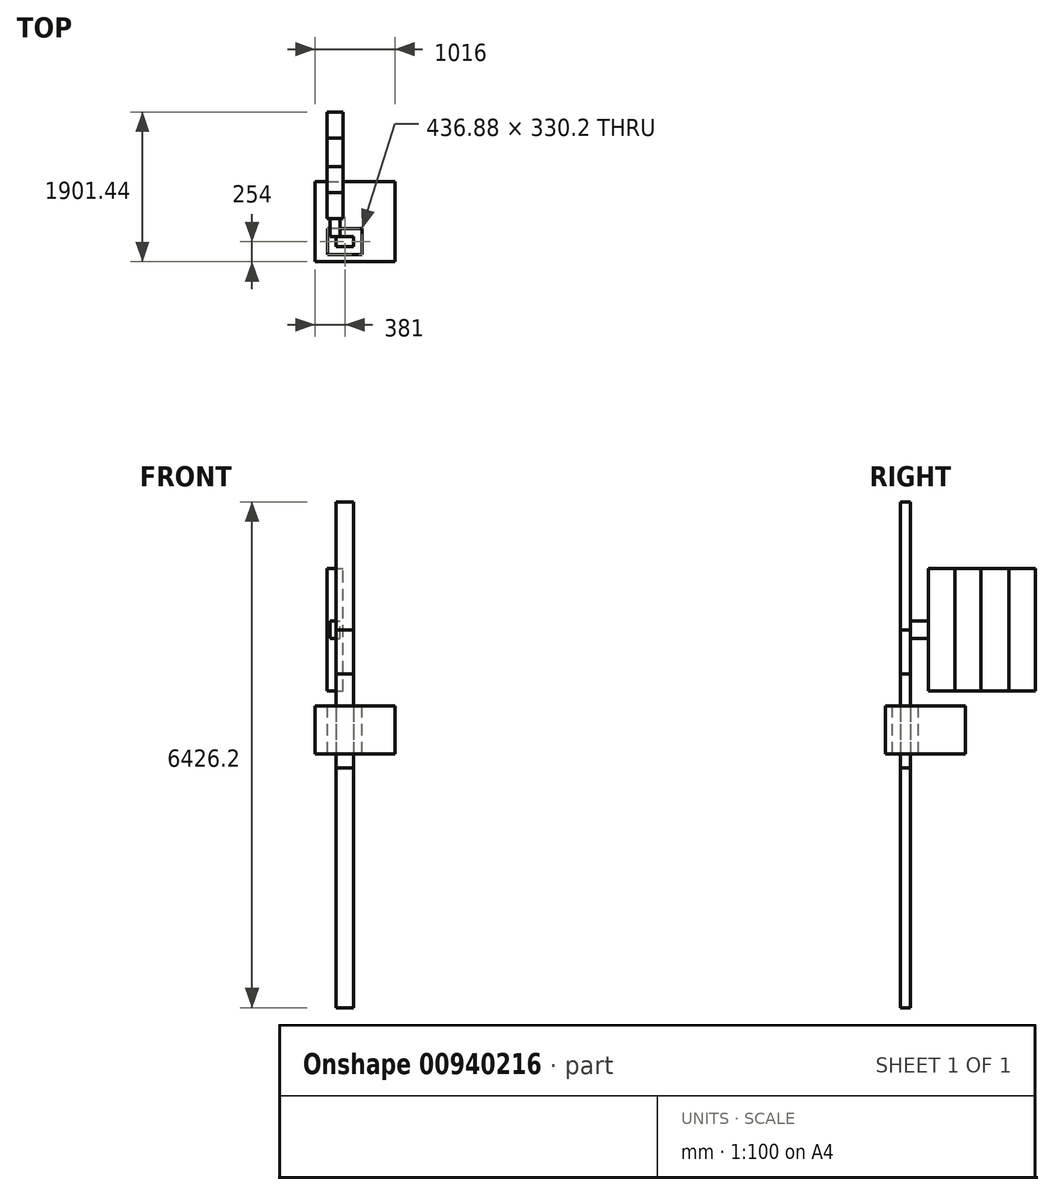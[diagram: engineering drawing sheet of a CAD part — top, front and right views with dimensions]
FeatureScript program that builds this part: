
annotation { "Feature Type Name" : "Feature", "Feature Type Description" : "" }
export const myFeature = defineFeature(function(context is Context, id is Id, definition is map)
    precondition{}
    {
        {
            var Q0;
            Q0=qCreatedBy(makeId("Top.planeOp"),FACE);
            var sketch = newSketch(context, id + "F0", { "sketchPlane" : qUnion([Q0])});
            skLineSegment(sketch, "E0.bottom", {"start": v(0, 0) * mm, "end": v(1016, 0) * mm});
            skLineSegment(sketch, "E0.top", {"start": v(0, 1016) * mm, "end": v(1016, 1016) * mm});
            skLineSegment(sketch, "E0.left", {"start": v(0, 0) * mm, "end": v(0, 1016) * mm});
            skLineSegment(sketch, "E0.right", {"start": v(1016, 0) * mm, "end": v(1016, 1016) * mm});
            skSolve(sketch);
        }
        {
            var Q0;
            Q0=makeQuery(id+"F0.imprint","IMPRINT",FACE,{"disambiguationData":[TD([[makeQuery(id+"F0.imprint","IMPRINT",EDGE,{"derivedFrom":sQuery(id+"F0.wireOp",EDGE,"E0.bottom")}),1.0]])]});
            extrude(context, id + "F1", {"entities" : qUnion([Q0]), "depth" : 609.6 * mm, "offsetDistance" : 25.4 * mm});
        }
        {
            var Q0;
            Q0=makeQuery(id+"F1.opExtrude","CAP_FACE",FACE,{"disambiguationData":[OSD([sQuery(id+"F0.wireOp",EDGE,"E0.bottom"),sQuery(id+"F0.wireOp",EDGE,"E0.top"),sQuery(id+"F0.wireOp",EDGE,"E0.left"),sQuery(id+"F0.wireOp",EDGE,"E0.right")])],"isStart":false});
            var sketch = newSketch(context, id + "F2", { "sketchPlane" : qUnion([Q0])});
            skLineSegment(sketch, "E1.bottom", {"start": v(0, 0) * mm, "end": v(381, 0) * mm, "construction": true});
            skLineSegment(sketch, "E1.top", {"start": v(0, 254) * mm, "end": v(381, 254) * mm, "construction": true});
            skLineSegment(sketch, "E1.left", {"start": v(0, 0) * mm, "end": v(0, 254) * mm, "construction": true});
            skLineSegment(sketch, "E1.right", {"start": v(381, 0) * mm, "end": v(381, 254) * mm, "construction": true});
            skLineSegment(sketch, "E2.bottom", {"start": v(491.5, 317.5) * mm, "end": v(270.51, 317.5) * mm});
            skLineSegment(sketch, "E2.top", {"start": v(491.5, 190.5) * mm, "end": v(270.51, 190.5) * mm});
            skLineSegment(sketch, "E2.left", {"start": v(491.5, 317.5) * mm, "end": v(491.5, 190.5) * mm});
            skLineSegment(sketch, "E2.right", {"start": v(270.51, 317.5) * mm, "end": v(270.51, 190.5) * mm});
            skPoint(sketch, "E2.middle", {"position": v(381, 254) * mm});
            skLineSegment(sketch, "E3.bottom", {"start": v(599.44, 419.1) * mm, "end": v(162.56, 419.1) * mm});
            skLineSegment(sketch, "E3.top", {"start": v(599.44, 88.9) * mm, "end": v(162.56, 88.9) * mm});
            skLineSegment(sketch, "E3.left", {"start": v(599.44, 419.1) * mm, "end": v(599.44, 88.9) * mm});
            skLineSegment(sketch, "E3.right", {"start": v(162.56, 419.1) * mm, "end": v(162.56, 88.9) * mm});
            skSolve(sketch);
        }
        {
            var Q0;
            Q0=makeQuery(id+"F2.imprint","IMPRINT",FACE,{"disambiguationData":[TD([[makeQuery(id+"F2.imprint","IMPRINT",EDGE,{"derivedFrom":sQuery(id+"F2.wireOp",EDGE,"E2.bottom")}),-1.0]])]});
            var Q1;
            Q1=makeQuery(id+"F2.imprint","IMPRINT",FACE,{"disambiguationData":[TD([[makeQuery(id+"F2.imprint","IMPRINT",EDGE,{"derivedFrom":sQuery(id+"F2.wireOp",EDGE,"E2.bottom")}),1.0]])]});
            extrude(context, id + "F3", {"entities" : qUnion([Q0, Q1]), "operationType" : NewBodyOperationType.REMOVE, "endBound" : BoundingType.THROUGH_ALL, "oppositeDirection" : true, "depth" : 25.4 * mm, "offsetDistance" : 25.4 * mm});
        }
        {
            var Q0;
            Q0=makeQuery(id+"F2.imprint","IMPRINT",FACE,{"disambiguationData":[TD([[makeQuery(id+"F2.imprint","IMPRINT",EDGE,{"derivedFrom":sQuery(id+"F2.wireOp",EDGE,"E2.bottom")}),1.0]])]});
            extrude(context, id + "F4", {"entities" : qUnion([Q0]), "depth" : 1524 * mm, "offsetDistance" : 25.4 * mm, "symmetric" : true});
        }
        {
            var Q0;
            Q0=makeQuery(id+"F4.opExtrude","CAP_FACE",FACE,{"disambiguationData":[OSD([sQuery(id+"F2.wireOp",EDGE,"E2.bottom"),sQuery(id+"F2.wireOp",EDGE,"E2.top"),sQuery(id+"F2.wireOp",EDGE,"E2.left"),sQuery(id+"F2.wireOp",EDGE,"E2.right")])],"isStart":true});
            extrude(context, id + "F5", {"entities" : qUnion([Q0]), "operationType" : NewBodyOperationType.ADD, "depth" : 1168.4 * mm, "offsetDistance" : 25.4 * mm});
        }
        {
            var Q0;
            Q0=makeQuery(id+"F4.opExtrude","CAP_FACE",FACE,{"disambiguationData":[OSD([sQuery(id+"F2.wireOp",EDGE,"E2.bottom"),sQuery(id+"F2.wireOp",EDGE,"E2.top"),sQuery(id+"F2.wireOp",EDGE,"E2.left"),sQuery(id+"F2.wireOp",EDGE,"E2.right")])],"isStart":false});
            extrude(context, id + "F6", {"entities" : qUnion([Q0]), "operationType" : NewBodyOperationType.ADD, "depth" : 431.8 * mm, "offsetDistance" : 25.4 * mm});
        }
        {
            var Q0;
            Q0=makeQuery(id+"F6.opExtrude","CAP_FACE",FACE,{"disambiguationData":[OSD([sQuery(id+"F2.wireOp",EDGE,"E2.bottom"),sQuery(id+"F2.wireOp",EDGE,"E2.top"),sQuery(id+"F2.wireOp",EDGE,"E2.left"),sQuery(id+"F2.wireOp",EDGE,"E2.right")])],"isStart":false});
            var Q1;
            Q1=makeQuery(id+"F1.opExtrude","CAP_FACE",FACE,{"disambiguationData":[OSD([sQuery(id+"F0.wireOp",EDGE,"E0.bottom"),sQuery(id+"F0.wireOp",EDGE,"E0.top"),sQuery(id+"F0.wireOp",EDGE,"E0.left"),sQuery(id+"F0.wireOp",EDGE,"E0.right")])],"isStart":false});
            extrude(context, id + "F7", {"entities" : qUnion([Q0]), "operationType" : NewBodyOperationType.REMOVE, "endBound" : BoundingType.UP_TO_SURFACE, "oppositeDirection" : true, "depth" : 25.4 * mm, "endBoundEntityFace" : qUnion([Q1]), "offsetDistance" : 25.4 * mm});
        }
        {
            var Q0;
            Q0=makeQuery(id+"F7.boolean.opBoolean","COPY",FACE,{"derivedFrom":makeQuery(id+"F7.opExtrude","CAP_FACE",FACE,{"disambiguationData":[OSD([sQuery(id+"F2.wireOp",EDGE,"E2.bottom"),sQuery(id+"F2.wireOp",EDGE,"E2.top"),sQuery(id+"F2.wireOp",EDGE,"E2.left"),sQuery(id+"F2.wireOp",EDGE,"E2.right")])],"isStart":false})});
            extrude(context, id + "F8", {"entities" : qUnion([Q0]), "operationType" : NewBodyOperationType.ADD, "depth" : 406.4 * mm, "offsetDistance" : 25.4 * mm});
        }
        {
            var Q0;
            Q0=makeQuery(id+"F5.opExtrude","CAP_FACE",FACE,{"disambiguationData":[OSD([sQuery(id+"F2.wireOp",EDGE,"E2.bottom"),sQuery(id+"F2.wireOp",EDGE,"E2.top"),sQuery(id+"F2.wireOp",EDGE,"E2.left"),sQuery(id+"F2.wireOp",EDGE,"E2.right")])],"isStart":false});
            var Q1;
            Q1=makeQuery(id+"F1.opExtrude","CAP_FACE",FACE,{"disambiguationData":[OSD([sQuery(id+"F0.wireOp",EDGE,"E0.bottom"),sQuery(id+"F0.wireOp",EDGE,"E0.top"),sQuery(id+"F0.wireOp",EDGE,"E0.left"),sQuery(id+"F0.wireOp",EDGE,"E0.right")])],"isStart":true});
            extrude(context, id + "F9", {"entities" : qUnion([Q0]), "operationType" : NewBodyOperationType.REMOVE, "endBound" : BoundingType.UP_TO_SURFACE, "oppositeDirection" : true, "depth" : 25.4 * mm, "endBoundEntityFace" : qUnion([Q1]), "offsetDistance" : 25.4 * mm});
        }
        {
            var Q0;
            Q0=makeQuery(id+"F9.boolean.opBoolean","COPY",FACE,{"derivedFrom":makeQuery(id+"F9.opExtrude","CAP_FACE",FACE,{"disambiguationData":[OSD([sQuery(id+"F2.wireOp",EDGE,"E2.bottom"),sQuery(id+"F2.wireOp",EDGE,"E2.top"),sQuery(id+"F2.wireOp",EDGE,"E2.left"),sQuery(id+"F2.wireOp",EDGE,"E2.right")])],"isStart":false})});
            extrude(context, id + "F10", {"entities" : qUnion([Q0]), "operationType" : NewBodyOperationType.ADD, "depth" : 177.8 * mm, "offsetDistance" : 25.4 * mm});
        }
        {
            var Q0;
            Q0=makeQuery(id+"F8.opExtrude","CAP_FACE",FACE,{"disambiguationData":[OSD([sQuery(id+"F2.wireOp",EDGE,"E2.bottom"),sQuery(id+"F2.wireOp",EDGE,"E2.top"),sQuery(id+"F2.wireOp",EDGE,"E2.left"),sQuery(id+"F2.wireOp",EDGE,"E2.right")])],"isStart":false});
            extrude(context, id + "F11", {"entities" : qUnion([Q0]), "depth" : 3048 * mm, "offsetDistance" : 25.4 * mm});
        }
        {
            var Q0;
            Q0=makeQuery(id+"F10.opExtrude","CAP_FACE",FACE,{"disambiguationData":[OSD([sQuery(id+"F2.wireOp",EDGE,"E2.bottom"),sQuery(id+"F2.wireOp",EDGE,"E2.top"),sQuery(id+"F2.wireOp",EDGE,"E2.left"),sQuery(id+"F2.wireOp",EDGE,"E2.right")])],"isStart":false});
            extrude(context, id + "F12", {"entities" : qUnion([Q0]), "depth" : 3048 * mm, "offsetDistance" : 25.4 * mm});
        }
        {
            var Q0;
            Q0=makeQuery(id+"F11.opExtrude","CAP_FACE",FACE,{"disambiguationData":[OSD([sQuery(id+"F2.wireOp",EDGE,"E2.bottom"),sQuery(id+"F2.wireOp",EDGE,"E2.top"),sQuery(id+"F2.wireOp",EDGE,"E2.left"),sQuery(id+"F2.wireOp",EDGE,"E2.right")])],"isStart":false});
            extrude(context, id + "F13", {"entities" : qUnion([Q0]), "operationType" : NewBodyOperationType.REMOVE, "oppositeDirection" : true, "depth" : 2489.2 * mm, "offsetDistance" : 25.4 * mm});
        }
        {
            var Q0;
            Q0=makeQuery(id+"F13.boolean.opBoolean","COPY",FACE,{"derivedFrom":makeQuery(id+"F13.opExtrude","CAP_FACE",FACE,{"disambiguationData":[OSD([sQuery(id+"F2.wireOp",EDGE,"E2.bottom"),sQuery(id+"F2.wireOp",EDGE,"E2.top"),sQuery(id+"F2.wireOp",EDGE,"E2.left"),sQuery(id+"F2.wireOp",EDGE,"E2.right")])],"isStart":false})});
            extrude(context, id + "F14", {"entities" : qUnion([Q0]), "depth" : 1625.6 * mm, "offsetDistance" : 25.4 * mm});
        }
        {
            var Q0;
            Q0=makeQuery(id+"F14.opExtrude","SWEPT_FACE",FACE,{"disambiguationData":[OSD([sQuery(id+"F2.wireOp",EDGE,"E2.right")])]});
            var sketch = newSketch(context, id + "F15", { "sketchPlane" : qUnion([Q0])});
            skLineSegment(sketch, "E4.bottom", {"start": v(-190.5, 1464.31) * mm, "end": v(-317.5, 1464.31) * mm});
            skLineSegment(sketch, "E4.top", {"start": v(-190.5, 1685.3) * mm, "end": v(-317.5, 1685.3) * mm});
            skLineSegment(sketch, "E4.left", {"start": v(-190.5, 1464.31) * mm, "end": v(-190.5, 1685.3) * mm});
            skLineSegment(sketch, "E4.right", {"start": v(-317.5, 1464.31) * mm, "end": v(-317.5, 1685.3) * mm});
            skPoint(sketch, "E4.middle", {"position": v(-254, 1574.8) * mm});
            skSolve(sketch);
        }
        {
            var Q0;
            Q0 = qSketchRegion(id + "F15", true);
            extrude(context, id + "F16", {"entities" : qUnion([Q0]), "depth" : 228.6 * mm, "offsetDistance" : 25.4 * mm});
        }
        {
            var Q0;
            Q0=makeQuery(id+"F16.opExtrude","CAP_FACE",FACE,{"disambiguationData":[OSD([sQuery(id+"F15.wireOp",EDGE,"E4.bottom"),sQuery(id+"F15.wireOp",EDGE,"E4.top"),sQuery(id+"F15.wireOp",EDGE,"E4.left"),sQuery(id+"F15.wireOp",EDGE,"E4.right")])],"isStart":false});
            var sketch = newSketch(context, id + "F17", { "sketchPlane" : qUnion([Q0])});
            skLineSegment(sketch, "E5.bottom", {"start": v(-151.26, 796.16) * mm, "end": v(-356.74, 796.16) * mm});
            skLineSegment(sketch, "E5.top", {"start": v(-151.26, 2353.44) * mm, "end": v(-356.74, 2353.44) * mm});
            skLineSegment(sketch, "E5.left", {"start": v(-151.26, 796.16) * mm, "end": v(-151.26, 2353.44) * mm});
            skLineSegment(sketch, "E5.right", {"start": v(-356.74, 796.16) * mm, "end": v(-356.74, 2353.44) * mm});
            skPoint(sketch, "E5.middle", {"position": v(-254, 1574.8) * mm});
            skPoint(sketch, "E5.middle.positionSnap0", {"position": v(-317.5, 1574.8) * mm});
            skPoint(sketch, "E5.middle.positionSnap1", {"position": v(-254, 1464.31) * mm});
            skPoint(sketch, "E5.centerSnap0", {"position": v(-317.5, 1574.8) * mm});
            skPoint(sketch, "E5.centerSnap1", {"position": v(-254, 1464.31) * mm});
            skSolve(sketch);
        }
        {
            var Q0;
            Q0 = qSketchRegion(id + "F17", true);
            extrude(context, id + "F18", {"entities" : qUnion([Q0]), "depth" : 332.5 * mm, "offsetDistance" : 25.4 * mm});
        }
        {
            var Q0;
            Q0=makeQuery(id+"F18.opExtrude","CAP_FACE",FACE,{"disambiguationData":[OSD([sQuery(id+"F17.wireOp",EDGE,"E5.bottom"),sQuery(id+"F17.wireOp",EDGE,"E5.top"),sQuery(id+"F17.wireOp",EDGE,"E5.left"),sQuery(id+"F17.wireOp",EDGE,"E5.right")])],"isStart":false});
            extrude(context, id + "F19", {"entities" : qUnion([Q0]), "depth" : 332.5 * mm, "offsetDistance" : 25.4 * mm});
        }
        {
            var Q0;
            Q0=makeQuery(id+"F19.opExtrude","CAP_FACE",FACE,{"disambiguationData":[OSD([sQuery(id+"F17.wireOp",EDGE,"E5.bottom"),sQuery(id+"F17.wireOp",EDGE,"E5.top"),sQuery(id+"F17.wireOp",EDGE,"E5.left"),sQuery(id+"F17.wireOp",EDGE,"E5.right")])],"isStart":false});
            extrude(context, id + "F20", {"entities" : qUnion([Q0]), "depth" : 332.5 * mm, "offsetDistance" : 25.4 * mm});
        }
        {
            var Q0;
            Q0=makeQuery(id+"F20.opExtrude","CAP_FACE",FACE,{"disambiguationData":[OSD([sQuery(id+"F17.wireOp",EDGE,"E5.bottom"),sQuery(id+"F17.wireOp",EDGE,"E5.top"),sQuery(id+"F17.wireOp",EDGE,"E5.left"),sQuery(id+"F17.wireOp",EDGE,"E5.right")])],"isStart":false});
            extrude(context, id + "F21", {"entities" : qUnion([Q0]), "operationType" : NewBodyOperationType.ADD, "depth" : 25.4 * mm, "offsetDistance" : 25.4 * mm});
        }
        {
            var Q0;
            Q0=makeQuery(id+"F21.opExtrude","CAP_FACE",FACE,{"disambiguationData":[OSD([sQuery(id+"F17.wireOp",EDGE,"E5.bottom"),sQuery(id+"F17.wireOp",EDGE,"E5.top"),sQuery(id+"F17.wireOp",EDGE,"E5.left"),sQuery(id+"F17.wireOp",EDGE,"E5.right")])],"isStart":false});
            extrude(context, id + "F22", {"entities" : qUnion([Q0]), "depth" : 332.5 * mm, "offsetDistance" : 25.4 * mm});
        }
    });
